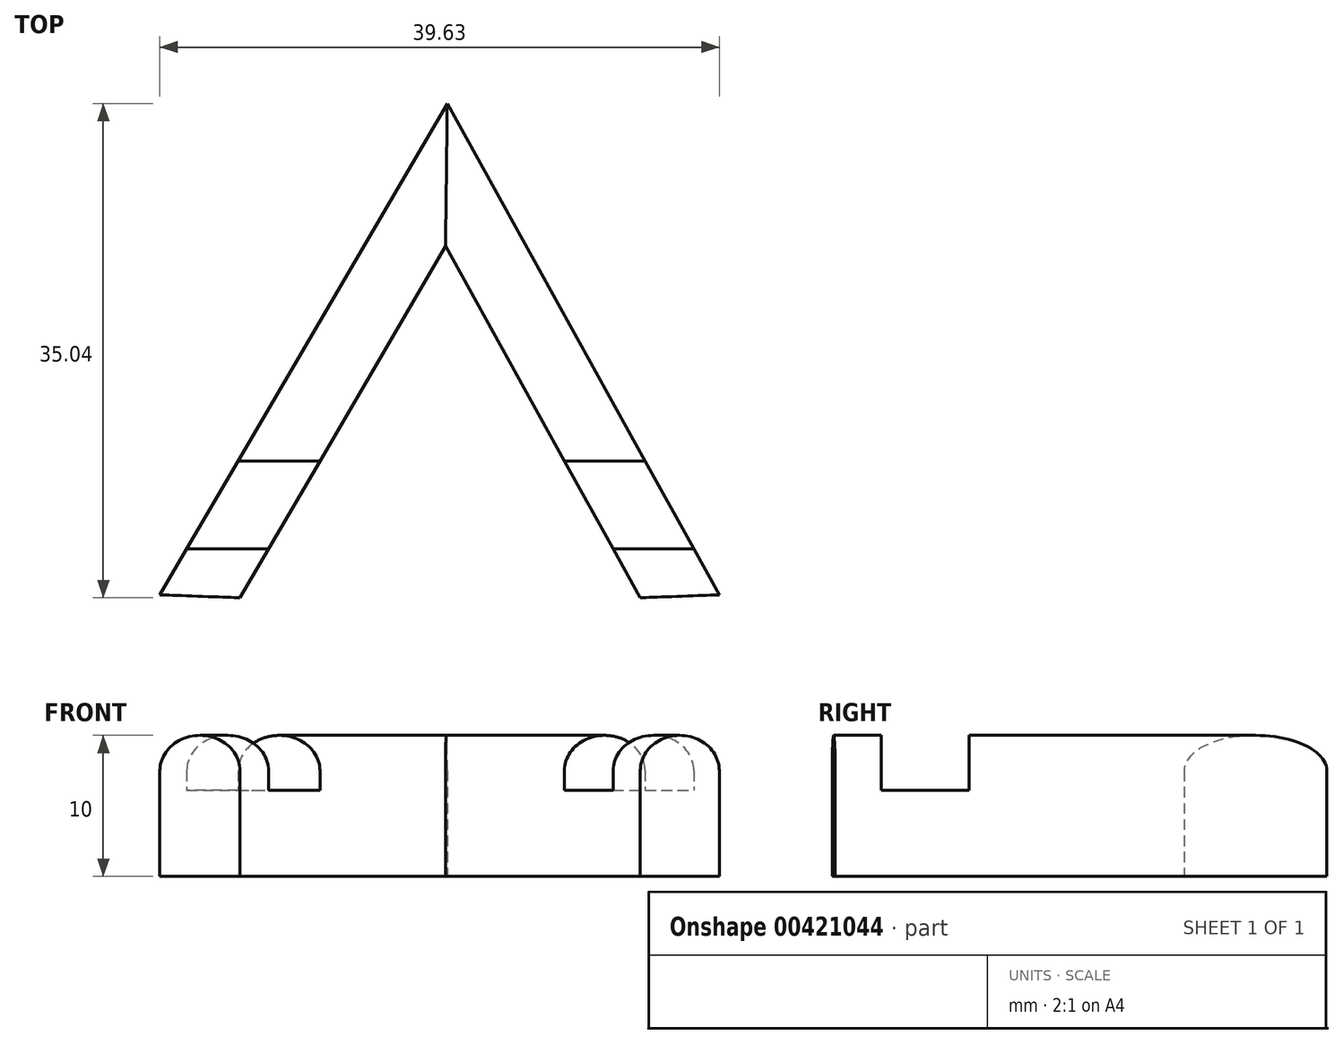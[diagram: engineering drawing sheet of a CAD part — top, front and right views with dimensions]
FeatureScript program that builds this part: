
annotation { "Feature Type Name" : "Feature", "Feature Type Description" : "" }
export const myFeature = defineFeature(function(context is Context, id is Id, definition is map)
    precondition{}
    {
        {
            var Q0;
            Q0=qCreatedBy(makeId("Top.planeOp"),FACE);
            var sketch = newSketch(context, id + "F0", { "sketchPlane" : qUnion([Q0])});
            skLineSegment(sketch, "E0", {"start": v(0, 0) * mm, "end": v(-14.57, -24.93) * mm});
            skLineSegment(sketch, "E1", {"start": v(0, 0) * mm, "end": v(13.79, -24.93) * mm});
            skLineSegment(sketch, "E2.0", {"start": v(0.12, 10.11) * mm, "end": v(-20.24, -24.72) * mm});
            skLineSegment(sketch, "E2.1", {"start": v(0.12, 10.11) * mm, "end": v(19.4, -24.72) * mm});
            skLineSegment(sketch, "E3", {"start": v(-20.24, -24.72) * mm, "end": v(-14.57, -24.93) * mm});
            skLineSegment(sketch, "E4", {"start": v(13.79, -24.93) * mm, "end": v(19.4, -24.72) * mm});
            skSolve(sketch);
        }
        {
            var Q0;
            Q0 = qSketchRegion(id + "F0", true);
            extrude(context, id + "F1", {"entities" : qUnion([Q0]), "depth" : 10 * mm});
        }
        {
            var Q0;
            Q0=makeQuery(id+"F1.opExtrude","CAP_FACE",FACE,{"disambiguationData":[OSD([sQuery(id+"F0.wireOp",EDGE,"E0"),sQuery(id+"F0.wireOp",EDGE,"E1"),sQuery(id+"F0.wireOp",EDGE,"E2.0"),sQuery(id+"F0.wireOp",EDGE,"E2.1"),sQuery(id+"F0.wireOp",EDGE,"E3"),sQuery(id+"F0.wireOp",EDGE,"E4")])],"isStart":false});
            var sketch = newSketch(context, id + "F2", { "sketchPlane" : qUnion([Q0])});
            skLineSegment(sketch, "E5.bottom", {"start": v(-22.31, -15.22) * mm, "end": v(26.66, -15.22) * mm});
            skLineSegment(sketch, "E5.top", {"start": v(-22.31, -21.46) * mm, "end": v(26.66, -21.46) * mm});
            skLineSegment(sketch, "E5.left", {"start": v(-22.31, -15.22) * mm, "end": v(-22.31, -21.46) * mm});
            skLineSegment(sketch, "E5.right", {"start": v(26.66, -15.22) * mm, "end": v(26.66, -21.46) * mm});
            skSolve(sketch);
        }
        {
            var Q0;
            Q0 = qSketchRegion(id + "F2", true);
            extrude(context, id + "F3", {"entities" : qUnion([Q0]), "operationType" : NewBodyOperationType.REMOVE, "oppositeDirection" : true, "depth" : 3.9 * mm});
        }
        {
            var Q0;
            {var subQ0=sQuery(id+"F0.wireOp",EDGE,"E2.1");var subQ1=sQuery(id+"F0.wireOp",EDGE,"E2.0");Q0=makeQuery(id+"F3.boolean.opBoolean","SPLIT",EDGE,{"disambiguationData":[TD([makeQuery(id+"F1.opExtrude","SWEPT_FACE",FACE,{"disambiguationData":[OSD([subQ0])]})])],"derivedFrom":makeQuery(id+"F1.opExtrude","CAP_EDGE",EDGE,{"disambiguationData":[OSD([subQ1])],"isStart":false})});}
            var Q1;
            {var subQ0=sQuery(id+"F0.wireOp",EDGE,"E2.1");var subQ1=sQuery(id+"F0.wireOp",EDGE,"E2.0");Q1=makeQuery(id+"F3.boolean.opBoolean","SPLIT",EDGE,{"disambiguationData":[TD([makeQuery(id+"F1.opExtrude","SWEPT_FACE",FACE,{"disambiguationData":[OSD([subQ1])]})])],"derivedFrom":makeQuery(id+"F1.opExtrude","CAP_EDGE",EDGE,{"disambiguationData":[OSD([subQ0])],"isStart":false})});}
            var Q2;
            {var subQ0=sQuery(id+"F0.wireOp",EDGE,"E0");var subQ1=sQuery(id+"F0.wireOp",EDGE,"E1");Q2=makeQuery(id+"F3.boolean.opBoolean","SPLIT",EDGE,{"disambiguationData":[TD([makeQuery(id+"F1.opExtrude","SWEPT_FACE",FACE,{"disambiguationData":[OSD([subQ1])]})])],"derivedFrom":makeQuery(id+"F1.opExtrude","CAP_EDGE",EDGE,{"disambiguationData":[OSD([subQ0])],"isStart":false})});}
            var Q3;
            {var subQ0=sQuery(id+"F0.wireOp",EDGE,"E0");var subQ1=sQuery(id+"F0.wireOp",EDGE,"E1");Q3=makeQuery(id+"F3.boolean.opBoolean","SPLIT",EDGE,{"disambiguationData":[TD([makeQuery(id+"F1.opExtrude","SWEPT_FACE",FACE,{"disambiguationData":[OSD([subQ0])]})])],"derivedFrom":makeQuery(id+"F1.opExtrude","CAP_EDGE",EDGE,{"disambiguationData":[OSD([subQ1])],"isStart":false})});}
            var Q4;
            {var subQ0=sQuery(id+"F0.wireOp",EDGE,"E3");var subQ1=sQuery(id+"F0.wireOp",EDGE,"E2.0");Q4=makeQuery(id+"F3.boolean.opBoolean","SPLIT",EDGE,{"disambiguationData":[TD([makeQuery(id+"F1.opExtrude","SWEPT_FACE",FACE,{"disambiguationData":[OSD([subQ0])]})])],"derivedFrom":makeQuery(id+"F1.opExtrude","CAP_EDGE",EDGE,{"disambiguationData":[OSD([subQ1])],"isStart":false})});}
            var Q5;
            {var subQ0=sQuery(id+"F0.wireOp",EDGE,"E0");var subQ1=sQuery(id+"F0.wireOp",EDGE,"E3");Q5=makeQuery(id+"F3.boolean.opBoolean","SPLIT",EDGE,{"disambiguationData":[TD([makeQuery(id+"F1.opExtrude","SWEPT_FACE",FACE,{"disambiguationData":[OSD([subQ1])]})])],"derivedFrom":makeQuery(id+"F1.opExtrude","CAP_EDGE",EDGE,{"disambiguationData":[OSD([subQ0])],"isStart":false})});}
            var Q6;
            {var subQ0=sQuery(id+"F0.wireOp",EDGE,"E4");var subQ1=sQuery(id+"F0.wireOp",EDGE,"E1");Q6=makeQuery(id+"F3.boolean.opBoolean","SPLIT",EDGE,{"disambiguationData":[TD([makeQuery(id+"F1.opExtrude","SWEPT_FACE",FACE,{"disambiguationData":[OSD([subQ0])]})])],"derivedFrom":makeQuery(id+"F1.opExtrude","CAP_EDGE",EDGE,{"disambiguationData":[OSD([subQ1])],"isStart":false})});}
            var Q7;
            {var subQ0=sQuery(id+"F0.wireOp",EDGE,"E4");var subQ1=sQuery(id+"F0.wireOp",EDGE,"E2.1");Q7=makeQuery(id+"F3.boolean.opBoolean","SPLIT",EDGE,{"disambiguationData":[TD([makeQuery(id+"F1.opExtrude","SWEPT_FACE",FACE,{"disambiguationData":[OSD([subQ0])]})])],"derivedFrom":makeQuery(id+"F1.opExtrude","CAP_EDGE",EDGE,{"disambiguationData":[OSD([subQ1])],"isStart":false})});}
            fillet(context, id + "F4", {"entities" : qUnion([Q0, Q1, Q2, Q3, Q4, Q5, Q6, Q7]), "radius" : 2.5 * mm, "tangentPropagation" : true, "allowEdgeOverflow" : false});
        }
    });
